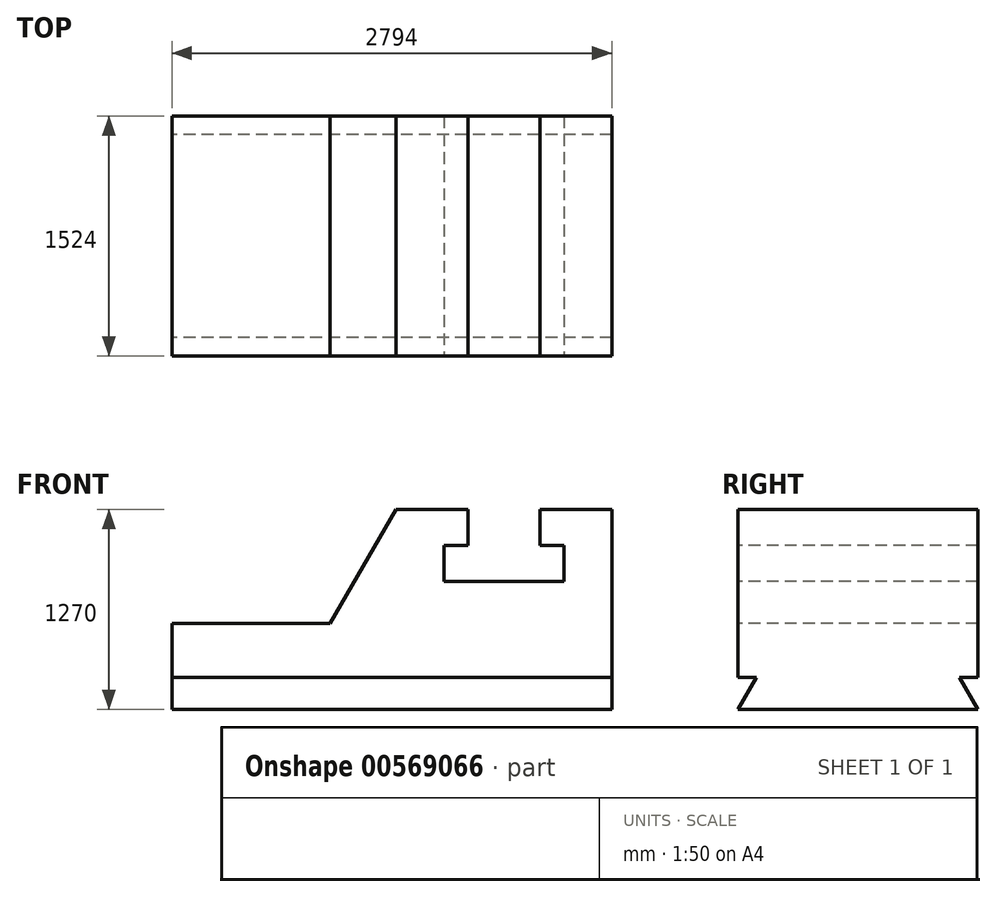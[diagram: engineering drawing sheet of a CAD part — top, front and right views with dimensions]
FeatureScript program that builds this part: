
annotation { "Feature Type Name" : "Feature", "Feature Type Description" : "" }
export const myFeature = defineFeature(function(context is Context, id is Id, definition is map)
    precondition{}
    {
        {
            var Q0;
            Q0=qCreatedBy(makeId("Top.planeOp"),FACE);
            var sketch = newSketch(context, id + "F0", { "sketchPlane" : qUnion([Q0])});
            skLineSegment(sketch, "E0", {"start": v(2677.8, 27.2) * mm, "end": v(-116.2, 27.2) * mm});
            skLineSegment(sketch, "E1", {"start": v(2677.8, 27.2) * mm, "end": v(2677.8, -1496.8) * mm});
            skLineSegment(sketch, "E2", {"start": v(2677.8, -1496.8) * mm, "end": v(-116.2, -1496.8) * mm});
            skLineSegment(sketch, "E3", {"start": v(-116.2, -1496.8) * mm, "end": v(-116.2, 27.2) * mm});
            skLineSegment(sketch, "E4", {"start": v(2677.8, 27.2) * mm, "end": v(2220.6, 27.2) * mm});
            skLineSegment(sketch, "E5", {"start": v(2220.6, 27.2) * mm, "end": v(2220.6, -1496.8) * mm});
            skLineSegment(sketch, "E6", {"start": v(2220.6, -1496.8) * mm, "end": v(1763.4, -1496.8) * mm});
            skLineSegment(sketch, "E7", {"start": v(1763.4, -1496.8) * mm, "end": v(1763.4, 27.2) * mm});
            skLineSegment(sketch, "E8", {"start": v(1763.4, 27.2) * mm, "end": v(1306.2, 27.2) * mm});
            skLineSegment(sketch, "E9", {"start": v(1306.2, 27.2) * mm, "end": v(1306.2, -1496.8) * mm});
            skSolve(sketch);
        }
        {
            var Q0;
            Q0 = qSketchRegion(id + "F0", true);
            extrude(context, id + "F1", {"entities" : qUnion([Q0]), "oppositeDirection" : true, "depth" : 1270 * mm, "offsetDistance" : 25.4 * mm});
        }
        {
            var Q0;
            Q0=makeQuery(id+"F1.opExtrude","SWEPT_FACE",FACE,{"disambiguationData":[OSD([sQuery(id+"F0.wireOp",EDGE,"E2"),sQuery(id+"F0.wireOp",EDGE,"E6")])]});
            var sketch = newSketch(context, id + "F2", { "sketchPlane" : qUnion([Q0])});
            skLineSegment(sketch, "E10", {"start": v(2677.8, 0) * mm, "end": v(2220.6, 0) * mm});
            skLineSegment(sketch, "E11", {"start": v(2220.6, 0) * mm, "end": v(1763.4, 0) * mm});
            skLineSegment(sketch, "E12", {"start": v(1763.4, 0) * mm, "end": v(1763.4, -228.6) * mm});
            skLineSegment(sketch, "E13", {"start": v(2220.6, 0) * mm, "end": v(2220.6, -228.6) * mm});
            skLineSegment(sketch, "E14", {"start": v(2220.6, -228.6) * mm, "end": v(2373, -228.6) * mm});
            skLineSegment(sketch, "E15", {"start": v(2373, -228.6) * mm, "end": v(2373, -457.2) * mm});
            skLineSegment(sketch, "E16", {"start": v(2373, -457.2) * mm, "end": v(1611, -457.2) * mm});
            skLineSegment(sketch, "E17", {"start": v(1611, -457.2) * mm, "end": v(1611, -228.6) * mm});
            skLineSegment(sketch, "E18", {"start": v(1611, -228.6) * mm, "end": v(1763.4, -228.6) * mm});
            skSolve(sketch);
        }
        {
            var Q0;
            Q0=makeQuery(id+"F2.imprint","IMPRINT",FACE,{"disambiguationData":[TD([[makeQuery(id+"F2.imprint","IMPRINT",EDGE,{"derivedFrom":sQuery(id+"F2.wireOp",EDGE,"E11")}),1.0]])]});
            extrude(context, id + "F3", {"entities" : qUnion([Q0]), "operationType" : NewBodyOperationType.REMOVE, "endBound" : BoundingType.THROUGH_ALL, "oppositeDirection" : true, "depth" : 25.4 * mm, "offsetDistance" : 25.4 * mm});
        }
        {
            var Q0;
            Q0=makeQuery(id+"F1.opExtrude","SWEPT_FACE",FACE,{"disambiguationData":[OSD([sQuery(id+"F0.wireOp",EDGE,"E3")])]});
            var sketch = newSketch(context, id + "F4", { "sketchPlane" : qUnion([Q0])});
            skLineSegment(sketch, "E19", {"start": v(1496.8, -1270) * mm, "end": v(601.76, 280.25) * mm});
            skLineSegment(sketch, "E20", {"start": v(-27.2, -1270) * mm, "end": v(867.83, 280.25) * mm});
            skLineSegment(sketch, "E21", {"start": v(-27.2, -1270) * mm, "end": v(-27.2, -1066.8) * mm});
            skLineSegment(sketch, "E22", {"start": v(-27.2, -1066.8) * mm, "end": v(1496.8, -1066.8) * mm});
            skLineSegment(sketch, "E23", {"start": v(1496.8, -1066.8) * mm, "end": v(1496.8, -1270) * mm});
            skSolve(sketch);
        }
        {
            var Q0;
            {var subQ0=sQuery(id+"F4.wireOp",EDGE,"E21");Q0=makeQuery(id+"F4.imprint","IMPRINT",FACE,{"disambiguationData":[TD([[makeQuery(id+"F4.imprint","IMPRINT",EDGE,{"derivedFrom":subQ0}),-1.0]])]});}
            extrude(context, id + "F5", {"entities" : qUnion([Q0]), "operationType" : NewBodyOperationType.REMOVE, "endBound" : BoundingType.THROUGH_ALL, "oppositeDirection" : true, "depth" : 25.4 * mm, "offsetDistance" : 25.4 * mm});
        }
        {
            var Q0;
            {var subQ0=sQuery(id+"F4.wireOp",EDGE,"E23");Q0=makeQuery(id+"F4.imprint","IMPRINT",FACE,{"disambiguationData":[TD([[makeQuery(id+"F4.imprint","IMPRINT",EDGE,{"derivedFrom":subQ0}),1.0]])]});}
            extrude(context, id + "F6", {"entities" : qUnion([Q0]), "operationType" : NewBodyOperationType.REMOVE, "endBound" : BoundingType.THROUGH_ALL, "oppositeDirection" : true, "depth" : 25.4 * mm, "offsetDistance" : 25.4 * mm});
        }
        {
            var Q0;
            Q0=makeQuery(id+"F1.opExtrude","SWEPT_FACE",FACE,{"disambiguationData":[OSD([sQuery(id+"F0.wireOp",EDGE,"E2"),sQuery(id+"F0.wireOp",EDGE,"E6")])]});
            var sketch = newSketch(context, id + "F7", { "sketchPlane" : qUnion([Q0])});
            skLineSegment(sketch, "E24", {"start": v(1763.4, 0) * mm, "end": v(1306.2, 0) * mm});
            skLineSegment(sketch, "E25", {"start": v(1306.2, 0) * mm, "end": v(888.16, -724.07) * mm});
            skLineSegment(sketch, "E26", {"start": v(888.16, -724.07) * mm, "end": v(-116.2, -724.07) * mm});
            skSolve(sketch);
        }
        {
            var Q0;
            {var subQ0=sQuery(id+"F7.wireOp",EDGE,"E25");Q0=makeQuery(id+"F7.imprint","IMPRINT",FACE,{"disambiguationData":[TD([[makeQuery(id+"F7.imprint","IMPRINT",EDGE,{"derivedFrom":subQ0}),-1.0]])]});}
            extrude(context, id + "F8", {"entities" : qUnion([Q0]), "operationType" : NewBodyOperationType.REMOVE, "endBound" : BoundingType.THROUGH_ALL, "oppositeDirection" : true, "depth" : 25.4 * mm, "offsetDistance" : 25.4 * mm});
        }
    });
